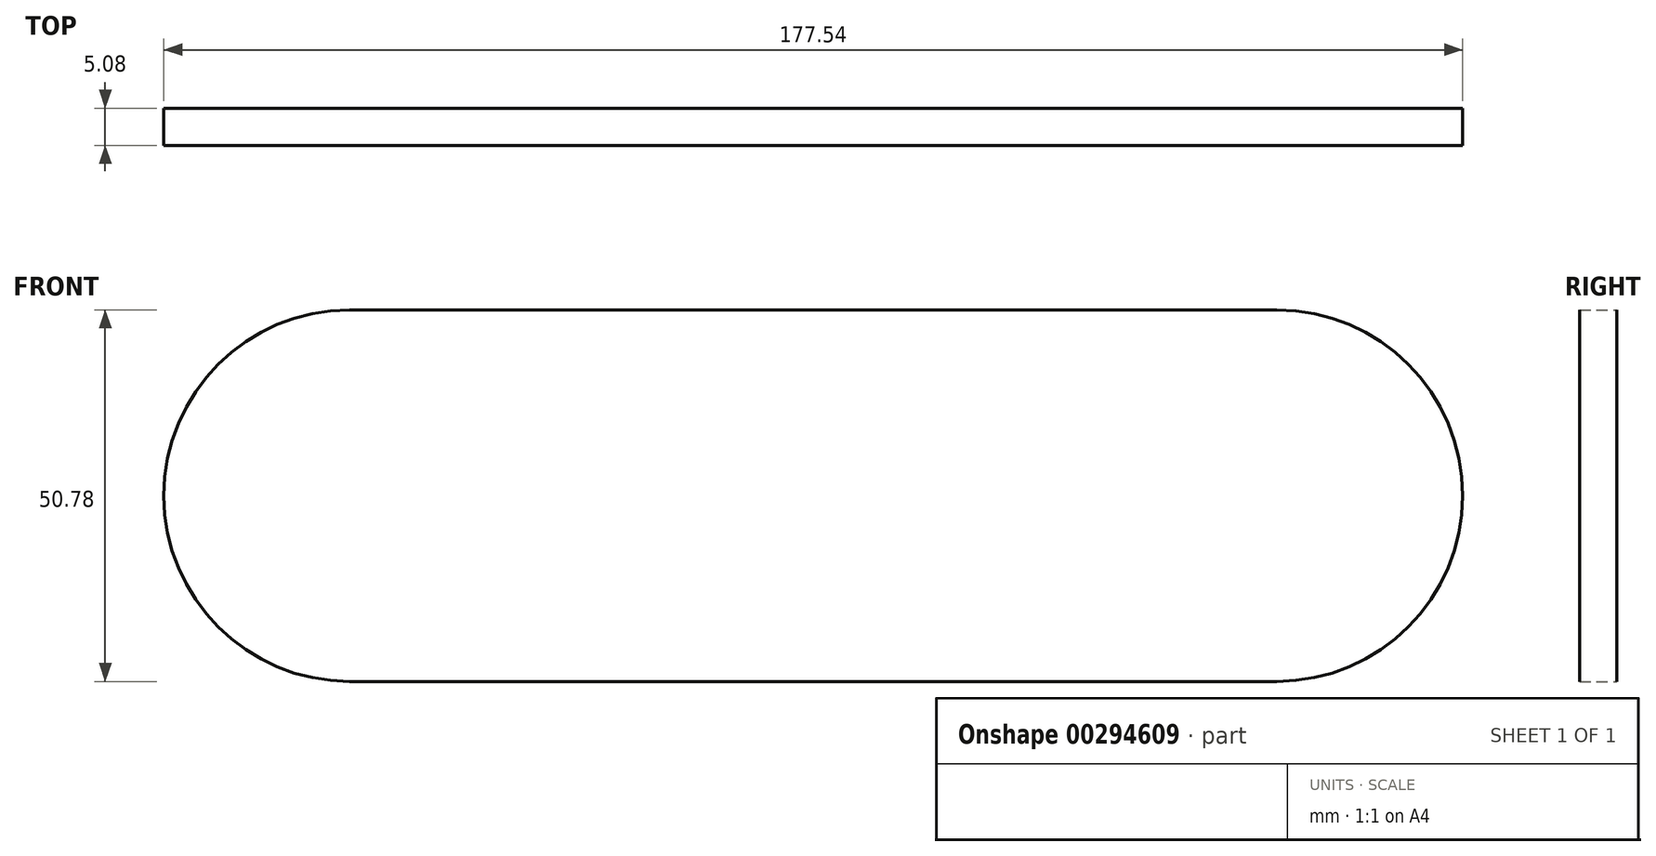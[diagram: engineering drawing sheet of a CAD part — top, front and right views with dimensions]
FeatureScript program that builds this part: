
annotation { "Feature Type Name" : "Feature", "Feature Type Description" : "" }
export const myFeature = defineFeature(function(context is Context, id is Id, definition is map)
    precondition{}
    {
        {
            var Q0;
            Q0=qCreatedBy(makeId("Front.planeOp"),FACE);
            var sketch = newSketch(context, id + "F0", { "sketchPlane" : qUnion([Q0])});
            skLineSegment(sketch, "E0.bottom", {"start": v(-63.37, 25.4) * mm, "end": v(63.37, 25.4) * mm});
            skLineSegment(sketch, "E1.MirrorCS", {"start": v(-63.37, -25.4) * mm, "end": v(63.37, -25.4) * mm});
            skPoint(sketch, "E2.endSnap0", {"position": v(-82.42, 0) * mm});
            skArc(sketch, "E3", {"start": v(-63.37, 25.4) * mm, "mid": v(-88.77, 0) * mm, "end": v(-63.37, -25.4) * mm});
            skArc(sketch, "E4", {"start": v(63.37, -25.4) * mm, "mid": v(88.77, 0) * mm, "end": v(63.37, 25.4) * mm});
            skArc(sketch, "E5", {"start": v(-2.33, -19.05) * mm, "mid": v(-1.84, -18.74) * mm, "end": v(-1.69, -18.18) * mm});
            skArc(sketch, "E6.MirrorCS", {"start": v(2.33, -19.05) * mm, "mid": v(1.84, -18.74) * mm, "end": v(1.69, -18.18) * mm});
            skFitSpline(sketch, "E7.0", {"points": [v(-1.58, -19) * mm, v(-1.68, -18.23) * mm, v(-1.8, -17.32) * mm, v(-1.8, -17.25) * mm, v(-1.8, -17.14) * mm, v(-1.8, -17.02) * mm, v(-1.78, -16.85) * mm, v(-1.75, -16.65) * mm, v(-1.7, -16.4) * mm, v(-1.63, -16.14) * mm, v(-1.54, -15.84) * mm, v(-1.42, -15.5) * mm, v(-1.26, -15.14) * mm, v(-1.08, -14.75) * mm, v(-0.86, -14.34) * mm, v(-0.68, -14.06) * mm, v(-0.6, -13.92) * mm]});
            skFitSpline(sketch, "E8.MirrorCS", {"points": [v(1.58, -19) * mm, v(1.68, -18.23) * mm, v(1.8, -17.32) * mm, v(1.8, -17.25) * mm, v(1.8, -17.14) * mm, v(1.8, -17.02) * mm, v(1.78, -16.85) * mm, v(1.75, -16.65) * mm, v(1.7, -16.4) * mm, v(1.63, -16.14) * mm, v(1.54, -15.84) * mm, v(1.42, -15.5) * mm, v(1.26, -15.14) * mm, v(1.08, -14.75) * mm, v(0.86, -14.34) * mm, v(0.68, -14.06) * mm, v(0.6, -13.92) * mm]});
            skLineSegment(sketch, "E9", {"start": v(0, 25.4) * mm, "end": v(0, 19.05) * mm, "construction": true});
            skLineSegment(sketch, "E10", {"start": v(-82.42, 0) * mm, "end": v(-88.77, 0) * mm, "construction": true});
            skLineSegment(sketch, "E11", {"start": v(88.77, 0) * mm, "end": v(82.42, 0) * mm, "construction": true});
            skLineSegment(sketch, "E12", {"start": v(-63.37, -25.4) * mm, "end": v(-63.37, -19.05) * mm, "construction": true});
            skLineSegment(sketch, "E13", {"start": v(63.37, -25.4) * mm, "end": v(63.37, -19.05) * mm, "construction": true});
            skLineSegment(sketch, "E14", {"start": v(-63.37, 25.4) * mm, "end": v(-63.37, 19.05) * mm, "construction": true});
            skLineSegment(sketch, "E15", {"start": v(63.37, 25.4) * mm, "end": v(63.37, 19.05) * mm, "construction": true});
            skArc(sketch, "E16", {"start": v(-63.37, 19.05) * mm, "mid": v(-82.42, 0) * mm, "end": v(-63.37, -19.05) * mm});
            skArc(sketch, "E17", {"start": v(63.37, -19.05) * mm, "mid": v(82.42, 0) * mm, "end": v(63.37, 19.05) * mm});
            skLineSegment(sketch, "E18", {"start": v(-63.37, 19.05) * mm, "end": v(63.37, 19.05) * mm});
            skLineSegment(sketch, "E19", {"start": v(-63.37, -19.05) * mm, "end": v(-15.1, -19.05) * mm});
            skLineSegment(sketch, "E20", {"start": v(2.33, -19.05) * mm, "end": v(4.05, -19.05) * mm});
            skArc(sketch, "E21.MirrorCS", {"start": v(4.05, -19.05) * mm, "mid": v(4.54, -18.74) * mm, "end": v(4.7, -18.18) * mm});
            skFitSpline(sketch, "E22.MirrorCS", {"points": [v(4.8, -19) * mm, v(4.7, -18.23) * mm, v(4.58, -17.32) * mm, v(4.58, -17.25) * mm, v(4.58, -17.14) * mm, v(4.59, -17.02) * mm, v(4.6, -16.85) * mm, v(4.64, -16.65) * mm, v(4.68, -16.4) * mm, v(4.75, -16.14) * mm, v(4.84, -15.84) * mm, v(4.97, -15.5) * mm, v(5.12, -15.14) * mm, v(5.3, -14.75) * mm, v(5.52, -14.34) * mm, v(5.7, -14.06) * mm, v(5.8, -13.92) * mm]});
            skFitSpline(sketch, "E23.MirrorCS", {"points": [v(7.96, -19) * mm, v(8.06, -18.23) * mm, v(8.18, -17.32) * mm, v(8.18, -17.25) * mm, v(8.18, -17.14) * mm, v(8.17, -17.02) * mm, v(8.16, -16.85) * mm, v(8.13, -16.65) * mm, v(8.08, -16.4) * mm, v(8.01, -16.14) * mm, v(7.92, -15.84) * mm, v(7.8, -15.5) * mm, v(7.64, -15.14) * mm, v(7.46, -14.75) * mm, v(7.24, -14.34) * mm, v(7.06, -14.06) * mm, v(6.97, -13.92) * mm]});
            skArc(sketch, "E24.MirrorCS", {"start": v(8.7, -19.05) * mm, "mid": v(8.22, -18.74) * mm, "end": v(8.07, -18.18) * mm});
            skArc(sketch, "E25.MirrorCS", {"start": v(-4.05, -19.05) * mm, "mid": v(-4.54, -18.74) * mm, "end": v(-4.7, -18.18) * mm});
            skFitSpline(sketch, "E26.MirrorCS", {"points": [v(-4.8, -19) * mm, v(-4.7, -18.23) * mm, v(-4.58, -17.32) * mm, v(-4.58, -17.25) * mm, v(-4.58, -17.14) * mm, v(-4.58, -17.02) * mm, v(-4.6, -16.85) * mm, v(-4.63, -16.65) * mm, v(-4.68, -16.4) * mm, v(-4.75, -16.14) * mm, v(-4.84, -15.84) * mm, v(-4.96, -15.5) * mm, v(-5.11, -15.14) * mm, v(-5.3, -14.75) * mm, v(-5.52, -14.34) * mm, v(-5.7, -14.06) * mm, v(-5.79, -13.92) * mm]});
            skFitSpline(sketch, "E27.MirrorCS", {"points": [v(-7.96, -19) * mm, v(-8.06, -18.23) * mm, v(-8.17, -17.32) * mm, v(-8.17, -17.25) * mm, v(-8.18, -17.14) * mm, v(-8.17, -17.02) * mm, v(-8.15, -16.85) * mm, v(-8.12, -16.65) * mm, v(-8.07, -16.4) * mm, v(-8, -16.14) * mm, v(-7.91, -15.84) * mm, v(-7.8, -15.5) * mm, v(-7.64, -15.14) * mm, v(-7.45, -14.75) * mm, v(-7.23, -14.34) * mm, v(-7.06, -14.06) * mm, v(-6.97, -13.92) * mm]});
            skArc(sketch, "E28.MirrorCS", {"start": v(-8.7, -19.05) * mm, "mid": v(-8.21, -18.74) * mm, "end": v(-8.06, -18.18) * mm});
            skLineSegment(sketch, "E29.MirrorCS", {"start": v(-6.38, -14.08) * mm, "end": v(-5.69, -14.08) * mm});
            skLineSegment(sketch, "E30.MirrorCS", {"start": v(-6.38, -14.08) * mm, "end": v(-7.07, -14.08) * mm});
            skLineSegment(sketch, "E31.trimOffspring", {"start": v(8.7, -19.05) * mm, "end": v(10.43, -19.05) * mm});
            skLineSegment(sketch, "E32.trimOffspring", {"start": v(-4.05, -19.05) * mm, "end": v(-2.33, -19.05) * mm});
            skLineSegment(sketch, "E33", {"start": v(-8.7, -19.05) * mm, "end": v(-9.58, -19.05) * mm, "construction": true});
            skArc(sketch, "E34.MirrorCS", {"start": v(-10.46, -19.05) * mm, "mid": v(-10.95, -18.74) * mm, "end": v(-11.1, -18.18) * mm});
            skFitSpline(sketch, "E35.MirrorCS", {"points": [v(-11.2, -19) * mm, v(-11.1, -18.23) * mm, v(-10.98, -17.32) * mm, v(-10.98, -17.25) * mm, v(-10.98, -17.14) * mm, v(-11, -17.02) * mm, v(-11, -16.85) * mm, v(-11.04, -16.65) * mm, v(-11.08, -16.4) * mm, v(-11.15, -16.14) * mm, v(-11.25, -15.84) * mm, v(-11.37, -15.5) * mm, v(-11.52, -15.14) * mm, v(-11.7, -14.75) * mm, v(-11.93, -14.34) * mm, v(-12.1, -14.06) * mm, v(-12.2, -13.92) * mm]});
            skLineSegment(sketch, "E36.MirrorCS", {"start": v(-12.78, -14.08) * mm, "end": v(-12.1, -14.08) * mm});
            skLineSegment(sketch, "E37.MirrorCS", {"start": v(-12.78, -14.08) * mm, "end": v(-13.47, -14.08) * mm});
            skFitSpline(sketch, "E38.MirrorCS", {"points": [v(-14.36, -19) * mm, v(-14.46, -18.23) * mm, v(-14.58, -17.32) * mm, v(-14.58, -17.25) * mm, v(-14.58, -17.14) * mm, v(-14.57, -17.02) * mm, v(-14.56, -16.85) * mm, v(-14.53, -16.65) * mm, v(-14.48, -16.4) * mm, v(-14.41, -16.14) * mm, v(-14.32, -15.84) * mm, v(-14.2, -15.5) * mm, v(-14.05, -15.14) * mm, v(-13.86, -14.75) * mm, v(-13.64, -14.34) * mm, v(-13.46, -14.06) * mm, v(-13.37, -13.92) * mm]});
            skArc(sketch, "E39.MirrorCS", {"start": v(-15.1, -19.05) * mm, "mid": v(-14.62, -18.74) * mm, "end": v(-14.47, -18.18) * mm});
            skArc(sketch, "E40.MirrorCS", {"start": v(10.43, -19.05) * mm, "mid": v(10.92, -18.74) * mm, "end": v(11.07, -18.18) * mm});
            skFitSpline(sketch, "E41.MirrorCS", {"points": [v(11.18, -19) * mm, v(11.08, -18.23) * mm, v(10.96, -17.32) * mm, v(10.96, -17.25) * mm, v(10.96, -17.14) * mm, v(10.96, -17.02) * mm, v(10.98, -16.85) * mm, v(11.01, -16.65) * mm, v(11.06, -16.4) * mm, v(11.13, -16.14) * mm, v(11.22, -15.84) * mm, v(11.34, -15.5) * mm, v(11.5, -15.14) * mm, v(11.68, -14.75) * mm, v(11.9, -14.34) * mm, v(12.08, -14.06) * mm, v(12.17, -13.92) * mm]});
            skFitSpline(sketch, "E42.MirrorCS", {"points": [v(14.34, -19) * mm, v(14.44, -18.23) * mm, v(14.55, -17.32) * mm, v(14.55, -17.25) * mm, v(14.56, -17.14) * mm, v(14.55, -17.02) * mm, v(14.53, -16.85) * mm, v(14.5, -16.65) * mm, v(14.45, -16.4) * mm, v(14.39, -16.14) * mm, v(14.3, -15.84) * mm, v(14.17, -15.5) * mm, v(14.02, -15.14) * mm, v(13.83, -14.75) * mm, v(13.61, -14.34) * mm, v(13.44, -14.06) * mm, v(13.35, -13.92) * mm]});
            skArc(sketch, "E43.MirrorCS", {"start": v(15.08, -19.05) * mm, "mid": v(14.6, -18.74) * mm, "end": v(14.44, -18.18) * mm});
            skLineSegment(sketch, "E44.trimOffspring", {"start": v(15.08, -19.05) * mm, "end": v(63.37, -19.05) * mm});
            skLineSegment(sketch, "E45.trimOffspring", {"start": v(-10.46, -19.05) * mm, "end": v(-8.7, -19.05) * mm});
            skLineSegment(sketch, "E46", {"start": v(-0.69, -14.08) * mm, "end": v(0.69, -14.08) * mm});
            skLineSegment(sketch, "E47.MirrorCS", {"start": v(3.88, 14.08) * mm, "end": v(2.5, 14.08) * mm});
            skFitSpline(sketch, "E48.MirrorCS", {"points": [v(1.61, 19) * mm, v(1.51, 18.23) * mm, v(1.4, 17.32) * mm, v(1.4, 17.25) * mm, v(1.4, 17.14) * mm, v(1.4, 17.02) * mm, v(1.41, 16.85) * mm, v(1.44, 16.65) * mm, v(1.5, 16.4) * mm, v(1.56, 16.14) * mm, v(1.65, 15.84) * mm, v(1.78, 15.5) * mm, v(1.93, 15.14) * mm, v(2.11, 14.75) * mm, v(2.33, 14.34) * mm, v(2.5, 14.06) * mm, v(2.6, 13.92) * mm]});
            skFitSpline(sketch, "E49.MirrorCS", {"points": [v(4.77, 19) * mm, v(4.87, 18.23) * mm, v(4.99, 17.32) * mm, v(4.99, 17.25) * mm, v(4.99, 17.14) * mm, v(4.98, 17.02) * mm, v(4.97, 16.85) * mm, v(4.94, 16.65) * mm, v(4.89, 16.4) * mm, v(4.82, 16.14) * mm, v(4.73, 15.84) * mm, v(4.6, 15.5) * mm, v(4.45, 15.14) * mm, v(4.27, 14.75) * mm, v(4.05, 14.34) * mm, v(3.87, 14.06) * mm, v(3.78, 13.92) * mm]});
            skArc(sketch, "E50.MirrorCS", {"start": v(5.52, 19.05) * mm, "mid": v(5.03, 18.74) * mm, "end": v(4.88, 18.18) * mm});
            skArc(sketch, "E51.MirrorCS", {"start": v(0.86, 19.05) * mm, "mid": v(1.35, 18.74) * mm, "end": v(1.5, 18.18) * mm});
            skArc(sketch, "E52.MirrorCS", {"start": v(-0.86, 19.05) * mm, "mid": v(-1.35, 18.74) * mm, "end": v(-1.5, 18.18) * mm});
            skArc(sketch, "E53.MirrorCS", {"start": v(-5.52, 19.05) * mm, "mid": v(-5.03, 18.74) * mm, "end": v(-4.88, 18.18) * mm});
            skFitSpline(sketch, "E54.MirrorCS", {"points": [v(-4.77, 19) * mm, v(-4.87, 18.23) * mm, v(-4.99, 17.32) * mm, v(-4.99, 17.25) * mm, v(-4.99, 17.14) * mm, v(-4.98, 17.02) * mm, v(-4.97, 16.85) * mm, v(-4.94, 16.65) * mm, v(-4.89, 16.4) * mm, v(-4.82, 16.14) * mm, v(-4.73, 15.84) * mm, v(-4.6, 15.5) * mm, v(-4.45, 15.14) * mm, v(-4.27, 14.75) * mm, v(-4.05, 14.34) * mm, v(-3.87, 14.06) * mm, v(-3.78, 13.92) * mm]});
            skFitSpline(sketch, "E55.MirrorCS", {"points": [v(-1.61, 19) * mm, v(-1.51, 18.23) * mm, v(-1.4, 17.32) * mm, v(-1.4, 17.25) * mm, v(-1.4, 17.14) * mm, v(-1.4, 17.02) * mm, v(-1.41, 16.85) * mm, v(-1.44, 16.65) * mm, v(-1.5, 16.4) * mm, v(-1.56, 16.14) * mm, v(-1.65, 15.84) * mm, v(-1.78, 15.5) * mm, v(-1.93, 15.14) * mm, v(-2.11, 14.75) * mm, v(-2.33, 14.34) * mm, v(-2.5, 14.06) * mm, v(-2.6, 13.92) * mm]});
            skLineSegment(sketch, "E56.MirrorCS", {"start": v(-3.88, 14.08) * mm, "end": v(-2.5, 14.08) * mm});
            skLineSegment(sketch, "E57", {"start": v(-5.52, 19.05) * mm, "end": v(-6.38, 19.05) * mm, "construction": true});
            skLineSegment(sketch, "E58", {"start": v(5.52, 19.05) * mm, "end": v(6.39, 19.05) * mm, "construction": true});
            skLineSegment(sketch, "E59", {"start": v(6.39, 19.05) * mm, "end": v(6.39, 17.76) * mm, "construction": true});
            skLineSegment(sketch, "E60", {"start": v(-6.38, 19.05) * mm, "end": v(-6.38, 18.26) * mm, "construction": true});
            skArc(sketch, "E61.MirrorCS", {"start": v(-7.24, 19.05) * mm, "mid": v(-7.73, 18.74) * mm, "end": v(-7.88, 18.18) * mm});
            skFitSpline(sketch, "E62.MirrorCS", {"points": [v(-7.99, 19) * mm, v(-7.89, 18.23) * mm, v(-7.77, 17.32) * mm, v(-7.77, 17.25) * mm, v(-7.77, 17.14) * mm, v(-7.77, 17.02) * mm, v(-7.8, 16.85) * mm, v(-7.82, 16.65) * mm, v(-7.87, 16.4) * mm, v(-7.94, 16.14) * mm, v(-8.03, 15.84) * mm, v(-8.15, 15.5) * mm, v(-8.3, 15.14) * mm, v(-8.49, 14.75) * mm, v(-8.7, 14.34) * mm, v(-8.89, 14.06) * mm, v(-8.98, 13.92) * mm]});
            skFitSpline(sketch, "E63.MirrorCS", {"points": [v(-11.14, 19) * mm, v(-11.25, 18.23) * mm, v(-11.36, 17.32) * mm, v(-11.36, 17.25) * mm, v(-11.36, 17.14) * mm, v(-11.36, 17.02) * mm, v(-11.34, 16.85) * mm, v(-11.31, 16.65) * mm, v(-11.26, 16.4) * mm, v(-11.2, 16.14) * mm, v(-11.1, 15.84) * mm, v(-10.98, 15.5) * mm, v(-10.83, 15.14) * mm, v(-10.64, 14.75) * mm, v(-10.42, 14.34) * mm, v(-10.25, 14.06) * mm, v(-10.16, 13.92) * mm]});
            skLineSegment(sketch, "E64.MirrorCS", {"start": v(-8.88, 14.08) * mm, "end": v(-10.26, 14.08) * mm});
            skArc(sketch, "E65.MirrorCS", {"start": v(-11.9, 19.05) * mm, "mid": v(-11.4, 18.74) * mm, "end": v(-11.25, 18.18) * mm});
            skArc(sketch, "E66.MirrorCS", {"start": v(7.26, 19.05) * mm, "mid": v(7.75, 18.74) * mm, "end": v(7.9, 18.18) * mm});
            skFitSpline(sketch, "E67.MirrorCS", {"points": [v(8, 19) * mm, v(7.9, 18.23) * mm, v(7.79, 17.32) * mm, v(7.79, 17.25) * mm, v(7.79, 17.14) * mm, v(7.8, 17.02) * mm, v(7.81, 16.85) * mm, v(7.84, 16.65) * mm, v(7.89, 16.4) * mm, v(7.96, 16.14) * mm, v(8.05, 15.84) * mm, v(8.17, 15.5) * mm, v(8.32, 15.14) * mm, v(8.5, 14.75) * mm, v(8.73, 14.34) * mm, v(8.9, 14.06) * mm, v(9, 13.92) * mm]});
            skArc(sketch, "E68.MirrorCS", {"start": v(11.91, 19.05) * mm, "mid": v(11.42, 18.74) * mm, "end": v(11.27, 18.18) * mm});
            skFitSpline(sketch, "E69.MirrorCS", {"points": [v(11.17, 19) * mm, v(11.27, 18.23) * mm, v(11.38, 17.32) * mm, v(11.38, 17.25) * mm, v(11.39, 17.14) * mm, v(11.38, 17.02) * mm, v(11.36, 16.85) * mm, v(11.33, 16.65) * mm, v(11.28, 16.4) * mm, v(11.22, 16.14) * mm, v(11.12, 15.84) * mm, v(11, 15.5) * mm, v(10.85, 15.14) * mm, v(10.66, 14.75) * mm, v(10.44, 14.34) * mm, v(10.27, 14.06) * mm, v(10.18, 13.92) * mm]});
            skLineSegment(sketch, "E70.MirrorCS", {"start": v(8.9, 14.08) * mm, "end": v(10.28, 14.08) * mm});
            skLineSegment(sketch, "E71", {"start": v(5.7, -14.08) * mm, "end": v(7.07, -14.08) * mm});
            skLineSegment(sketch, "E72", {"start": v(12.07, -14.08) * mm, "end": v(13.45, -14.08) * mm});
            skFitSpline(sketch, "E73.MirrorCS", {"points": [v(59.48, -25.44) * mm, v(59.38, -26.2) * mm, v(59.26, -27.11) * mm, v(59.26, -27.19) * mm, v(59.26, -27.3) * mm, v(59.26, -27.42) * mm, v(59.28, -27.59) * mm, v(59.3, -27.79) * mm, v(59.36, -28.03) * mm, v(59.43, -28.3) * mm, v(59.52, -28.6) * mm, v(59.64, -28.94) * mm, v(59.8, -29.3) * mm, v(59.98, -29.68) * mm, v(60.2, -30.1) * mm, v(60.37, -30.37) * mm, v(60.46, -30.52) * mm]});
            skArc(sketch, "E74.MirrorCS", {"start": v(58.73, -25.4) * mm, "mid": v(59.22, -25.7) * mm, "end": v(59.37, -26.26) * mm});
            skArc(sketch, "E75.MirrorCS", {"start": v(63.38, -25.4) * mm, "mid": v(62.9, -25.7) * mm, "end": v(62.74, -26.26) * mm});
            skFitSpline(sketch, "E76.MirrorCS", {"points": [v(62.63, -25.44) * mm, v(62.73, -26.2) * mm, v(62.85, -27.11) * mm, v(62.85, -27.19) * mm, v(62.85, -27.3) * mm, v(62.85, -27.42) * mm, v(62.83, -27.59) * mm, v(62.8, -27.79) * mm, v(62.75, -28.03) * mm, v(62.68, -28.3) * mm, v(62.6, -28.6) * mm, v(62.47, -28.94) * mm, v(62.32, -29.3) * mm, v(62.13, -29.68) * mm, v(61.91, -30.1) * mm, v(61.73, -30.37) * mm, v(61.65, -30.52) * mm]});
            skLineSegment(sketch, "E77.MirrorCS", {"start": v(61.74, -30.36) * mm, "end": v(60.36, -30.36) * mm});
            skLineSegment(sketch, "E78", {"start": v(58.73, -25.4) * mm, "end": v(57.88, -25.4) * mm, "construction": true});
            skLineSegment(sketch, "E79", {"start": v(57.88, -25.4) * mm, "end": v(57.88, -26.66) * mm, "construction": true});
            skArc(sketch, "E80.MirrorCS", {"start": v(57.02, -25.4) * mm, "mid": v(56.53, -25.7) * mm, "end": v(56.38, -26.26) * mm});
            skFitSpline(sketch, "E81.MirrorCS", {"points": [v(56.28, -25.44) * mm, v(56.38, -26.2) * mm, v(56.5, -27.11) * mm, v(56.5, -27.19) * mm, v(56.5, -27.3) * mm, v(56.49, -27.42) * mm, v(56.47, -27.59) * mm, v(56.44, -27.79) * mm, v(56.4, -28.03) * mm, v(56.33, -28.3) * mm, v(56.23, -28.6) * mm, v(56.11, -28.94) * mm, v(55.96, -29.3) * mm, v(55.77, -29.68) * mm, v(55.55, -30.1) * mm, v(55.38, -30.37) * mm, v(55.29, -30.52) * mm]});
            skLineSegment(sketch, "E82.MirrorCS", {"start": v(54, -30.36) * mm, "end": v(55.39, -30.36) * mm});
            skFitSpline(sketch, "E83.MirrorCS", {"points": [v(53.12, -25.44) * mm, v(53.02, -26.2) * mm, v(52.9, -27.11) * mm, v(52.9, -27.19) * mm, v(52.9, -27.3) * mm, v(52.9, -27.42) * mm, v(52.92, -27.59) * mm, v(52.95, -27.79) * mm, v(53, -28.03) * mm, v(53.07, -28.3) * mm, v(53.16, -28.6) * mm, v(53.28, -28.94) * mm, v(53.43, -29.3) * mm, v(53.62, -29.68) * mm, v(53.84, -30.1) * mm, v(54.02, -30.37) * mm, v(54.1, -30.52) * mm]});
            skArc(sketch, "E84.MirrorCS", {"start": v(52.37, -25.4) * mm, "mid": v(52.86, -25.7) * mm, "end": v(53.01, -26.26) * mm});
            skLineSegment(sketch, "E85", {"start": v(52.37, -25.4) * mm, "end": v(51.5, -25.4) * mm, "construction": true});
            skLineSegment(sketch, "E86", {"start": v(51.5, -25.4) * mm, "end": v(51.5, -27.12) * mm, "construction": true});
            skArc(sketch, "E87.MirrorCS", {"start": v(50.64, -25.4) * mm, "mid": v(50.15, -25.7) * mm, "end": v(50, -26.26) * mm});
            skFitSpline(sketch, "E88.MirrorCS", {"points": [v(49.89, -25.44) * mm, v(49.99, -26.2) * mm, v(50.1, -27.11) * mm, v(50.1, -27.19) * mm, v(50.1, -27.3) * mm, v(50.1, -27.42) * mm, v(50.09, -27.59) * mm, v(50.06, -27.79) * mm, v(50, -28.03) * mm, v(49.94, -28.3) * mm, v(49.85, -28.6) * mm, v(49.73, -28.94) * mm, v(49.57, -29.3) * mm, v(49.39, -29.68) * mm, v(49.17, -30.1) * mm, v(49, -30.37) * mm, v(48.9, -30.52) * mm]});
            skFitSpline(sketch, "E89.MirrorCS", {"points": [v(46.73, -25.44) * mm, v(46.63, -26.2) * mm, v(46.51, -27.11) * mm, v(46.51, -27.19) * mm, v(46.51, -27.3) * mm, v(46.52, -27.42) * mm, v(46.53, -27.59) * mm, v(46.56, -27.79) * mm, v(46.61, -28.03) * mm, v(46.68, -28.3) * mm, v(46.77, -28.6) * mm, v(46.9, -28.94) * mm, v(47.05, -29.3) * mm, v(47.23, -29.68) * mm, v(47.45, -30.1) * mm, v(47.63, -30.37) * mm, v(47.72, -30.52) * mm]});
            skArc(sketch, "E90.MirrorCS", {"start": v(45.98, -25.4) * mm, "mid": v(46.47, -25.7) * mm, "end": v(46.62, -26.26) * mm});
            skLineSegment(sketch, "E91.MirrorCS", {"start": v(49, -30.36) * mm, "end": v(47.62, -30.36) * mm});
            skFitSpline(sketch, "E92.MirrorCS", {"points": [v(62.63, 25.44) * mm, v(62.73, 26.2) * mm, v(62.85, 27.11) * mm, v(62.85, 27.19) * mm, v(62.85, 27.3) * mm, v(62.85, 27.42) * mm, v(62.83, 27.59) * mm, v(62.8, 27.79) * mm, v(62.75, 28.03) * mm, v(62.68, 28.3) * mm, v(62.6, 28.6) * mm, v(62.47, 28.94) * mm, v(62.32, 29.3) * mm, v(62.13, 29.68) * mm, v(61.91, 30.1) * mm, v(61.73, 30.37) * mm, v(61.65, 30.52) * mm]});
            skFitSpline(sketch, "E93.MirrorCS", {"points": [v(59.48, 25.44) * mm, v(59.38, 26.2) * mm, v(59.26, 27.11) * mm, v(59.26, 27.19) * mm, v(59.26, 27.3) * mm, v(59.26, 27.42) * mm, v(59.28, 27.59) * mm, v(59.3, 27.79) * mm, v(59.36, 28.03) * mm, v(59.43, 28.3) * mm, v(59.52, 28.6) * mm, v(59.64, 28.94) * mm, v(59.8, 29.3) * mm, v(59.98, 29.68) * mm, v(60.2, 30.1) * mm, v(60.37, 30.37) * mm, v(60.46, 30.52) * mm]});
            skArc(sketch, "E94.MirrorCS", {"start": v(63.38, 25.4) * mm, "mid": v(62.9, 25.7) * mm, "end": v(62.74, 26.26) * mm});
            skArc(sketch, "E95.MirrorCS", {"start": v(58.73, 25.4) * mm, "mid": v(59.22, 25.7) * mm, "end": v(59.37, 26.26) * mm});
            skArc(sketch, "E96.MirrorCS", {"start": v(57.02, 25.4) * mm, "mid": v(56.53, 25.7) * mm, "end": v(56.38, 26.26) * mm});
            skFitSpline(sketch, "E97.MirrorCS", {"points": [v(56.28, 25.44) * mm, v(56.38, 26.2) * mm, v(56.5, 27.11) * mm, v(56.5, 27.19) * mm, v(56.5, 27.3) * mm, v(56.49, 27.42) * mm, v(56.47, 27.59) * mm, v(56.44, 27.79) * mm, v(56.4, 28.03) * mm, v(56.33, 28.3) * mm, v(56.23, 28.6) * mm, v(56.11, 28.94) * mm, v(55.96, 29.3) * mm, v(55.77, 29.68) * mm, v(55.55, 30.1) * mm, v(55.38, 30.37) * mm, v(55.29, 30.52) * mm]});
            skLineSegment(sketch, "E98.MirrorCS", {"start": v(54, 30.36) * mm, "end": v(55.39, 30.36) * mm});
            skFitSpline(sketch, "E99.MirrorCS", {"points": [v(53.12, 25.44) * mm, v(53.02, 26.2) * mm, v(52.9, 27.11) * mm, v(52.9, 27.19) * mm, v(52.9, 27.3) * mm, v(52.9, 27.42) * mm, v(52.92, 27.59) * mm, v(52.95, 27.79) * mm, v(53, 28.03) * mm, v(53.07, 28.3) * mm, v(53.16, 28.6) * mm, v(53.28, 28.94) * mm, v(53.43, 29.3) * mm, v(53.62, 29.68) * mm, v(53.84, 30.1) * mm, v(54.02, 30.37) * mm, v(54.1, 30.52) * mm]});
            skArc(sketch, "E100.MirrorCS", {"start": v(52.37, 25.4) * mm, "mid": v(52.86, 25.7) * mm, "end": v(53.01, 26.26) * mm});
            skArc(sketch, "E101.MirrorCS", {"start": v(50.64, 25.4) * mm, "mid": v(50.15, 25.7) * mm, "end": v(50, 26.26) * mm});
            skFitSpline(sketch, "E102.MirrorCS", {"points": [v(49.89, 25.44) * mm, v(49.99, 26.2) * mm, v(50.1, 27.11) * mm, v(50.1, 27.19) * mm, v(50.1, 27.3) * mm, v(50.1, 27.42) * mm, v(50.09, 27.59) * mm, v(50.06, 27.79) * mm, v(50, 28.03) * mm, v(49.94, 28.3) * mm, v(49.85, 28.6) * mm, v(49.73, 28.94) * mm, v(49.57, 29.3) * mm, v(49.39, 29.68) * mm, v(49.17, 30.1) * mm, v(49, 30.37) * mm, v(48.9, 30.52) * mm]});
            skLineSegment(sketch, "E103.MirrorCS", {"start": v(49, 30.36) * mm, "end": v(47.62, 30.36) * mm});
            skFitSpline(sketch, "E104.MirrorCS", {"points": [v(46.73, 25.44) * mm, v(46.63, 26.2) * mm, v(46.51, 27.11) * mm, v(46.51, 27.19) * mm, v(46.51, 27.3) * mm, v(46.52, 27.42) * mm, v(46.53, 27.59) * mm, v(46.56, 27.79) * mm, v(46.61, 28.03) * mm, v(46.68, 28.3) * mm, v(46.77, 28.6) * mm, v(46.9, 28.94) * mm, v(47.05, 29.3) * mm, v(47.23, 29.68) * mm, v(47.45, 30.1) * mm, v(47.63, 30.37) * mm, v(47.72, 30.52) * mm]});
            skArc(sketch, "E105.MirrorCS", {"start": v(45.98, 25.4) * mm, "mid": v(46.47, 25.7) * mm, "end": v(46.62, 26.26) * mm});
            skLineSegment(sketch, "E106.MirrorCS", {"start": v(61.74, 30.36) * mm, "end": v(60.36, 30.36) * mm});
            skArc(sketch, "E107.MirrorCS", {"start": v(-45.98, -25.4) * mm, "mid": v(-46.47, -25.7) * mm, "end": v(-46.62, -26.26) * mm});
            skFitSpline(sketch, "E108.MirrorCS", {"points": [v(-46.73, -25.44) * mm, v(-46.63, -26.2) * mm, v(-46.51, -27.11) * mm, v(-46.51, -27.19) * mm, v(-46.51, -27.3) * mm, v(-46.52, -27.42) * mm, v(-46.53, -27.59) * mm, v(-46.56, -27.79) * mm, v(-46.61, -28.03) * mm, v(-46.68, -28.3) * mm, v(-46.77, -28.6) * mm, v(-46.9, -28.94) * mm, v(-47.05, -29.3) * mm, v(-47.23, -29.68) * mm, v(-47.45, -30.1) * mm, v(-47.63, -30.37) * mm, v(-47.72, -30.52) * mm]});
            skLineSegment(sketch, "E109.MirrorCS", {"start": v(-49, -30.36) * mm, "end": v(-47.62, -30.36) * mm});
            skFitSpline(sketch, "E110.MirrorCS", {"points": [v(-49.89, -25.44) * mm, v(-49.99, -26.2) * mm, v(-50.1, -27.11) * mm, v(-50.1, -27.19) * mm, v(-50.1, -27.3) * mm, v(-50.1, -27.42) * mm, v(-50.09, -27.59) * mm, v(-50.06, -27.79) * mm, v(-50, -28.03) * mm, v(-49.94, -28.3) * mm, v(-49.85, -28.6) * mm, v(-49.73, -28.94) * mm, v(-49.57, -29.3) * mm, v(-49.39, -29.68) * mm, v(-49.17, -30.1) * mm, v(-49, -30.37) * mm, v(-48.9, -30.52) * mm]});
            skArc(sketch, "E111.MirrorCS", {"start": v(-50.64, -25.4) * mm, "mid": v(-50.15, -25.7) * mm, "end": v(-50, -26.26) * mm});
            skArc(sketch, "E112.MirrorCS", {"start": v(-52.37, -25.4) * mm, "mid": v(-52.86, -25.7) * mm, "end": v(-53.01, -26.26) * mm});
            skFitSpline(sketch, "E113.MirrorCS", {"points": [v(-53.12, -25.44) * mm, v(-53.02, -26.2) * mm, v(-52.9, -27.11) * mm, v(-52.9, -27.19) * mm, v(-52.9, -27.3) * mm, v(-52.9, -27.42) * mm, v(-52.92, -27.59) * mm, v(-52.95, -27.79) * mm, v(-53, -28.03) * mm, v(-53.07, -28.3) * mm, v(-53.16, -28.6) * mm, v(-53.28, -28.94) * mm, v(-53.43, -29.3) * mm, v(-53.62, -29.68) * mm, v(-53.84, -30.1) * mm, v(-54.02, -30.37) * mm, v(-54.1, -30.52) * mm]});
            skLineSegment(sketch, "E114.MirrorCS", {"start": v(-54, -30.36) * mm, "end": v(-55.39, -30.36) * mm});
            skFitSpline(sketch, "E115.MirrorCS", {"points": [v(-56.28, -25.44) * mm, v(-56.38, -26.2) * mm, v(-56.5, -27.11) * mm, v(-56.5, -27.19) * mm, v(-56.5, -27.3) * mm, v(-56.49, -27.42) * mm, v(-56.47, -27.59) * mm, v(-56.44, -27.79) * mm, v(-56.4, -28.03) * mm, v(-56.33, -28.3) * mm, v(-56.23, -28.6) * mm, v(-56.11, -28.94) * mm, v(-55.96, -29.3) * mm, v(-55.77, -29.68) * mm, v(-55.55, -30.1) * mm, v(-55.38, -30.37) * mm, v(-55.29, -30.52) * mm]});
            skArc(sketch, "E116.MirrorCS", {"start": v(-57.02, -25.4) * mm, "mid": v(-56.53, -25.7) * mm, "end": v(-56.38, -26.26) * mm});
            skArc(sketch, "E117.MirrorCS", {"start": v(-58.73, -25.4) * mm, "mid": v(-59.22, -25.7) * mm, "end": v(-59.37, -26.26) * mm});
            skFitSpline(sketch, "E118.MirrorCS", {"points": [v(-59.48, -25.44) * mm, v(-59.38, -26.2) * mm, v(-59.26, -27.11) * mm, v(-59.26, -27.19) * mm, v(-59.26, -27.3) * mm, v(-59.26, -27.42) * mm, v(-59.28, -27.59) * mm, v(-59.3, -27.79) * mm, v(-59.36, -28.03) * mm, v(-59.43, -28.3) * mm, v(-59.52, -28.6) * mm, v(-59.64, -28.94) * mm, v(-59.8, -29.3) * mm, v(-59.98, -29.68) * mm, v(-60.2, -30.1) * mm, v(-60.37, -30.37) * mm, v(-60.46, -30.52) * mm]});
            skLineSegment(sketch, "E119.MirrorCS", {"start": v(-61.74, -30.36) * mm, "end": v(-60.36, -30.36) * mm});
            skFitSpline(sketch, "E120.MirrorCS", {"points": [v(-62.63, -25.44) * mm, v(-62.73, -26.2) * mm, v(-62.85, -27.11) * mm, v(-62.85, -27.19) * mm, v(-62.85, -27.3) * mm, v(-62.85, -27.42) * mm, v(-62.83, -27.59) * mm, v(-62.8, -27.79) * mm, v(-62.75, -28.03) * mm, v(-62.68, -28.3) * mm, v(-62.6, -28.6) * mm, v(-62.47, -28.94) * mm, v(-62.32, -29.3) * mm, v(-62.13, -29.68) * mm, v(-61.91, -30.1) * mm, v(-61.73, -30.37) * mm, v(-61.65, -30.52) * mm]});
            skArc(sketch, "E121.MirrorCS", {"start": v(-63.38, -25.4) * mm, "mid": v(-62.9, -25.7) * mm, "end": v(-62.74, -26.26) * mm});
            skFitSpline(sketch, "E122.MirrorCS", {"points": [v(-46.73, 25.44) * mm, v(-46.63, 26.2) * mm, v(-46.51, 27.11) * mm, v(-46.51, 27.19) * mm, v(-46.51, 27.3) * mm, v(-46.52, 27.42) * mm, v(-46.53, 27.59) * mm, v(-46.56, 27.79) * mm, v(-46.61, 28.03) * mm, v(-46.68, 28.3) * mm, v(-46.77, 28.6) * mm, v(-46.9, 28.94) * mm, v(-47.05, 29.3) * mm, v(-47.23, 29.68) * mm, v(-47.45, 30.1) * mm, v(-47.63, 30.37) * mm, v(-47.72, 30.52) * mm]});
            skArc(sketch, "E123.MirrorCS", {"start": v(-45.98, 25.4) * mm, "mid": v(-46.47, 25.7) * mm, "end": v(-46.62, 26.26) * mm});
            skArc(sketch, "E124.MirrorCS", {"start": v(-50.64, 25.4) * mm, "mid": v(-50.15, 25.7) * mm, "end": v(-50, 26.26) * mm});
            skFitSpline(sketch, "E125.MirrorCS", {"points": [v(-49.89, 25.44) * mm, v(-49.99, 26.2) * mm, v(-50.1, 27.11) * mm, v(-50.1, 27.19) * mm, v(-50.1, 27.3) * mm, v(-50.1, 27.42) * mm, v(-50.09, 27.59) * mm, v(-50.06, 27.79) * mm, v(-50, 28.03) * mm, v(-49.94, 28.3) * mm, v(-49.85, 28.6) * mm, v(-49.73, 28.94) * mm, v(-49.57, 29.3) * mm, v(-49.39, 29.68) * mm, v(-49.17, 30.1) * mm, v(-49, 30.37) * mm, v(-48.9, 30.52) * mm]});
            skLineSegment(sketch, "E126.MirrorCS", {"start": v(-49, 30.36) * mm, "end": v(-47.62, 30.36) * mm});
            skLineSegment(sketch, "E127.MirrorCS", {"start": v(-54, 30.36) * mm, "end": v(-55.39, 30.36) * mm});
            skFitSpline(sketch, "E128.MirrorCS", {"points": [v(-53.12, 25.44) * mm, v(-53.02, 26.2) * mm, v(-52.9, 27.11) * mm, v(-52.9, 27.19) * mm, v(-52.9, 27.3) * mm, v(-52.9, 27.42) * mm, v(-52.92, 27.59) * mm, v(-52.95, 27.79) * mm, v(-53, 28.03) * mm, v(-53.07, 28.3) * mm, v(-53.16, 28.6) * mm, v(-53.28, 28.94) * mm, v(-53.43, 29.3) * mm, v(-53.62, 29.68) * mm, v(-53.84, 30.1) * mm, v(-54.02, 30.37) * mm, v(-54.1, 30.52) * mm]});
            skFitSpline(sketch, "E129.MirrorCS", {"points": [v(-56.28, 25.44) * mm, v(-56.38, 26.2) * mm, v(-56.5, 27.11) * mm, v(-56.5, 27.19) * mm, v(-56.5, 27.3) * mm, v(-56.49, 27.42) * mm, v(-56.47, 27.59) * mm, v(-56.44, 27.79) * mm, v(-56.4, 28.03) * mm, v(-56.33, 28.3) * mm, v(-56.23, 28.6) * mm, v(-56.11, 28.94) * mm, v(-55.96, 29.3) * mm, v(-55.77, 29.68) * mm, v(-55.55, 30.1) * mm, v(-55.38, 30.37) * mm, v(-55.29, 30.52) * mm]});
            skArc(sketch, "E130.MirrorCS", {"start": v(-52.37, 25.4) * mm, "mid": v(-52.86, 25.7) * mm, "end": v(-53.01, 26.26) * mm});
            skArc(sketch, "E131.MirrorCS", {"start": v(-57.02, 25.4) * mm, "mid": v(-56.53, 25.7) * mm, "end": v(-56.38, 26.26) * mm});
            skFitSpline(sketch, "E132.MirrorCS", {"points": [v(-59.48, 25.44) * mm, v(-59.38, 26.2) * mm, v(-59.26, 27.11) * mm, v(-59.26, 27.19) * mm, v(-59.26, 27.3) * mm, v(-59.26, 27.42) * mm, v(-59.28, 27.59) * mm, v(-59.3, 27.79) * mm, v(-59.36, 28.03) * mm, v(-59.43, 28.3) * mm, v(-59.52, 28.6) * mm, v(-59.64, 28.94) * mm, v(-59.8, 29.3) * mm, v(-59.98, 29.68) * mm, v(-60.2, 30.1) * mm, v(-60.37, 30.37) * mm, v(-60.46, 30.52) * mm]});
            skArc(sketch, "E133.MirrorCS", {"start": v(-58.73, 25.4) * mm, "mid": v(-59.22, 25.7) * mm, "end": v(-59.37, 26.26) * mm});
            skArc(sketch, "E134.MirrorCS", {"start": v(-63.38, 25.4) * mm, "mid": v(-62.9, 25.7) * mm, "end": v(-62.74, 26.26) * mm});
            skFitSpline(sketch, "E135.MirrorCS", {"points": [v(-62.63, 25.44) * mm, v(-62.73, 26.2) * mm, v(-62.85, 27.11) * mm, v(-62.85, 27.19) * mm, v(-62.85, 27.3) * mm, v(-62.85, 27.42) * mm, v(-62.83, 27.59) * mm, v(-62.8, 27.79) * mm, v(-62.75, 28.03) * mm, v(-62.68, 28.3) * mm, v(-62.6, 28.6) * mm, v(-62.47, 28.94) * mm, v(-62.32, 29.3) * mm, v(-62.13, 29.68) * mm, v(-61.91, 30.1) * mm, v(-61.73, 30.37) * mm, v(-61.65, 30.52) * mm]});
            skLineSegment(sketch, "E136.MirrorCS", {"start": v(-61.74, 30.36) * mm, "end": v(-60.36, 30.36) * mm});
            skLineSegment(sketch, "E137", {"start": v(54.7, -30.36) * mm, "end": v(54.7, -25.4) * mm, "construction": true});
            skSolve(sketch);
        }
        {
            var Q0;
            Q0 = qSketchRegion(id + "F0", true);
            var Q1;
            {var subQ0=sQuery(id+"F0.wireOp",EDGE,"E61.MirrorCS");Q1=makeQuery(id+"F0.imprint","IMPRINT",FACE,{"disambiguationData":[TD([[makeQuery(id+"F0.imprint","IMPRINT",EDGE,{"derivedFrom":subQ0}),-1.0]])]});}
            var Q2;
            {var subQ1=sQuery(id+"F0.wireOp",EDGE,"E52.MirrorCS");Q2=makeQuery(id+"F0.imprint","IMPRINT",FACE,{"disambiguationData":[TD([[makeQuery(id+"F0.imprint","IMPRINT",EDGE,{"derivedFrom":subQ1}),-1.0]])]});}
            var Q3;
            Q3=makeQuery(id+"F0.imprint","IMPRINT",FACE,{"disambiguationData":[TD([[makeQuery(id+"F0.imprint","IMPRINT",EDGE,{"derivedFrom":sQuery(id+"F0.wireOp",EDGE,"E47.MirrorCS")}),-1.0]])]});
            var Q4;
            {var subQ1=sQuery(id+"F0.wireOp",EDGE,"E66.MirrorCS");Q4=makeQuery(id+"F0.imprint","IMPRINT",FACE,{"disambiguationData":[TD([[makeQuery(id+"F0.imprint","IMPRINT",EDGE,{"derivedFrom":subQ1}),1.0]])]});}
            extrude(context, id + "F1", {"entities" : qUnion([Q0, Q1, Q2, Q3, Q4]), "depth" : 5.08 * mm});
        }
    });
